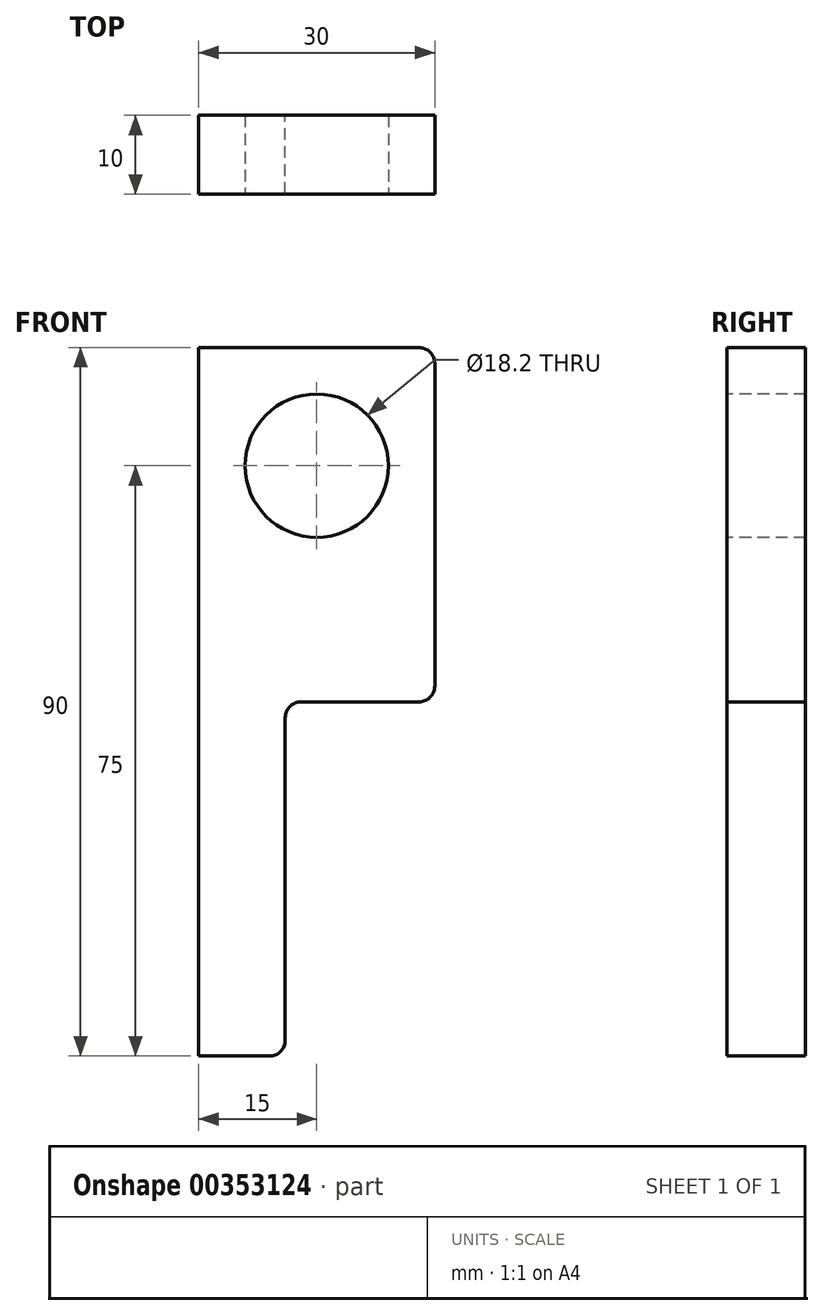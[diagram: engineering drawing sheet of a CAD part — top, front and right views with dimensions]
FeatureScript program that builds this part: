
annotation { "Feature Type Name" : "Feature", "Feature Type Description" : "" }
export const myFeature = defineFeature(function(context is Context, id is Id, definition is map)
    precondition{}
    {
        {
            var Q0;
            Q0=qCreatedBy(makeId("Front.planeOp"),FACE);
            var sketch = newSketch(context, id + "F0", { "sketchPlane" : qUnion([Q0])});
            skLineSegment(sketch, "E0", {"start": v(0, 0) * mm, "end": v(-30, 0) * mm});
            skLineSegment(sketch, "E1", {"start": v(-30, 0) * mm, "end": v(-30, -90) * mm});
            skLineSegment(sketch, "E2", {"start": v(-30, -90) * mm, "end": v(-19, -90) * mm});
            skLineSegment(sketch, "E3", {"start": v(-19, -90) * mm, "end": v(-19, -45) * mm});
            skLineSegment(sketch, "E4", {"start": v(-19, -45) * mm, "end": v(0, -45) * mm});
            skLineSegment(sketch, "E5", {"start": v(0, -45) * mm, "end": v(0, 0) * mm});
            skSolve(sketch);
        }
        {
            var Q0;
            Q0=makeQuery(id+"F0.imprint","IMPRINT",FACE,{"disambiguationData":[TD([[makeQuery(id+"F0.imprint","IMPRINT",EDGE,{"derivedFrom":sQuery(id+"F0.wireOp",EDGE,"E0")}),1.0]])]});
            extrude(context, id + "F1", {"entities" : qUnion([Q0]), "depth" : 10 * mm});
        }
        {
            var Q0;
            Q0=makeQuery(id+"F1.opExtrude","SWEPT_EDGE",EDGE,{"disambiguationData":[OSD([sQuery(id+"F0.wireOp",EDGE,"E2"),sQuery(id+"F0.wireOp",EDGE,"E3")])]});
            var Q1;
            Q1=makeQuery(id+"F1.opExtrude","SWEPT_EDGE",EDGE,{"disambiguationData":[OSD([sQuery(id+"F0.wireOp",EDGE,"E4"),sQuery(id+"F0.wireOp",EDGE,"E5")])]});
            var Q2;
            Q2=makeQuery(id+"F1.opExtrude","SWEPT_EDGE",EDGE,{"disambiguationData":[OSD([sQuery(id+"F0.wireOp",EDGE,"E3"),sQuery(id+"F0.wireOp",EDGE,"E4")])]});
            var Q3;
            Q3=makeQuery(id+"F1.opExtrude","SWEPT_EDGE",EDGE,{"disambiguationData":[OSD([sQuery(id+"F0.wireOp",EDGE,"E0"),sQuery(id+"F0.wireOp",EDGE,"E5")])]});
            fillet(context, id + "F2", {"entities" : qUnion([Q0, Q1, Q2, Q3]), "radius" : 2 * mm, "tangentPropagation" : true, "allowEdgeOverflow" : false});
        }
        {
            var Q0;
            Q0=makeQuery(id+"F1.opExtrude","CAP_FACE",FACE,{"disambiguationData":[OSD([sQuery(id+"F0.wireOp",EDGE,"E0"),sQuery(id+"F0.wireOp",EDGE,"E1"),sQuery(id+"F0.wireOp",EDGE,"E2"),sQuery(id+"F0.wireOp",EDGE,"E3"),sQuery(id+"F0.wireOp",EDGE,"E4"),sQuery(id+"F0.wireOp",EDGE,"E5")])],"isStart":false});
            var sketch = newSketch(context, id + "F3", { "sketchPlane" : qUnion([Q0])});
            skCircle(sketch, "E6", {"center": v(-15, -15) * mm, "radius": 9.1 * mm});
            skSolve(sketch);
        }
        {
            var Q0;
            Q0=makeQuery(id+"F3.imprint","IMPRINT",FACE,{"disambiguationData":[TD([[makeQuery(id+"F3.imprint","IMPRINT",EDGE,{"derivedFrom":sQuery(id+"F3.wireOp",EDGE,"E6")}),1.0]])]});
            extrude(context, id + "F4", {"entities" : qUnion([Q0]), "operationType" : NewBodyOperationType.REMOVE, "oppositeDirection" : true, "depth" : 25 * mm});
        }
    });
